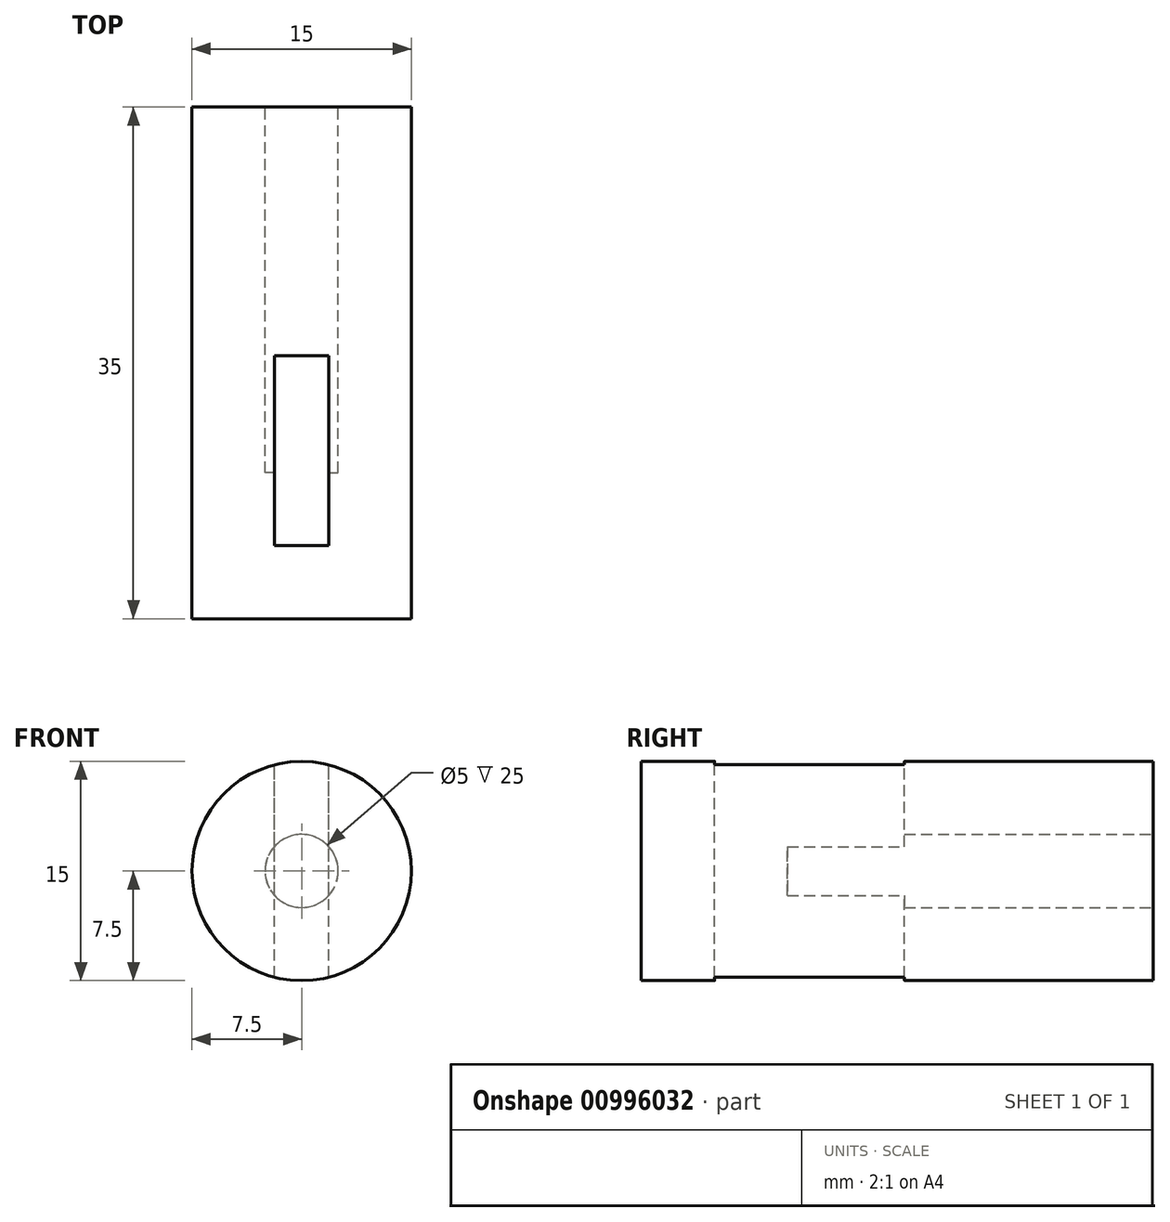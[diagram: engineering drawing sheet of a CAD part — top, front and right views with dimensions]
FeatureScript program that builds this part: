
annotation { "Feature Type Name" : "Feature", "Feature Type Description" : "" }
export const myFeature = defineFeature(function(context is Context, id is Id, definition is map)
    precondition{}
    {
        {
            var Q0;
            Q0=qCreatedBy(makeId("Front.planeOp"),FACE);
            var sketch = newSketch(context, id + "F0", { "sketchPlane" : qUnion([Q0])});
            skCircle(sketch, "E0", {"center": v(0, 0) * mm, "radius": 7.5 * mm});
            skSolve(sketch);
        }
        {
            var Q0;
            Q0 = qSketchRegion(id + "F0", true);
            extrude(context, id + "F1", {"entities" : qUnion([Q0]), "depth" : 35 * mm, "offsetDistance" : 25 * mm});
        }
        {
            var Q0;
            Q0=qCreatedBy(makeId("Top.planeOp"),FACE);
            var sketch = newSketch(context, id + "F2", { "sketchPlane" : qUnion([Q0])});
            skLineSegment(sketch, "E1.bottom", {"start": v(1.86, -29.98) * mm, "end": v(-1.86, -29.98) * mm});
            skLineSegment(sketch, "E1.top", {"start": v(1.86, -17) * mm, "end": v(-1.86, -17) * mm});
            skLineSegment(sketch, "E1.left", {"start": v(1.86, -29.98) * mm, "end": v(1.86, -17) * mm});
            skLineSegment(sketch, "E1.right", {"start": v(-1.86, -29.98) * mm, "end": v(-1.86, -17) * mm});
            skPoint(sketch, "E1.middle", {"position": v(0, -23.49) * mm});
            skSolve(sketch);
        }
        {
            var Q0;
            Q0 = qSketchRegion(id + "F2", true);
            extrude(context, id + "F3", {"entities" : qUnion([Q0]), "operationType" : NewBodyOperationType.REMOVE, "endBound" : BoundingType.SYMMETRIC, "oppositeDirection" : true, "depth" : 25 * mm, "offsetDistance" : 25 * mm});
        }
        {
            var Q0;
            Q0=makeQuery(id+"F1.opExtrude","CAP_FACE",FACE,{"disambiguationData":[OSD([sQuery(id+"F0.wireOp",EDGE,"E0")])],"isStart":true});
            var sketch = newSketch(context, id + "F4", { "sketchPlane" : qUnion([Q0])});
            skCircle(sketch, "E2", {"center": v(0, 0) * mm, "radius": 2.5 * mm});
            skSolve(sketch);
        }
        {
            var Q0;
            Q0 = qSketchRegion(id + "F4", true);
            extrude(context, id + "F5", {"entities" : qUnion([Q0]), "operationType" : NewBodyOperationType.REMOVE, "oppositeDirection" : true, "depth" : 25 * mm, "offsetDistance" : 25 * mm});
        }
    });
